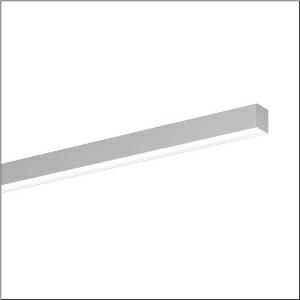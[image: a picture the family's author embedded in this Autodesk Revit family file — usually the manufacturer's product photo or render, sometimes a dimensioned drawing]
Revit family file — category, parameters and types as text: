
# Revit family: silica_21_51mx23dc4asb
name_source: partatom
category: Lighting Fixtures
units: mm (PartAtom-declared; Revit-internal decimal feet)

## family parameters
Cut with Voids When Loaded = No
Host = Face
Light Source = No
Part Type = Normal
Room Calculation Point = No
Round Connector Dimension = Use Diameter
Shared = No

## types (1)
- --- (1 x LED, 8200 lm, 58.2 W, 4000K)
    Apparent Load = 58 VA
    CIE Flux Codes = 78 96 99 100 100
    Color Rendering = 80
    Color Temperature = 4000K
    Default Elevation = 1800 mm
    Description = Silica 21, office luminaire, primary optical cover: prismatic diffuser, of PMMA, CAT 2 (L<= 3000cd/m²), light emission: direct distribution, primary light characteristic: symmetric, installation type: surface-mounted, LED, rated luminous flux: 8.200lm, luminous efficacy: 141lm/W, light colour: 840, colour temperature: 4000K, control gear: DALI 2, with terminal, 3+2-pole, max. 2.5mm², mains connection: 220..240V, AC, 50/60Hz, rated input power: 58.2W, luminaire housing, of aluminium, metallic grey (RAL 9006), length: 3.004mm, width: 53mm, height: 53mm, protection rating (complete): IP20, insulation class (complete): insulation class I (protective earthing), certification: CE, permissible operating ambient temperature: 0..+35°C, standard: EN 50419, packaging unit: 1 piece
    Height = 53 mm
    Lamp = 1 x LED
    Lamp Light Flux = 8200 lm
    Lamp Power = 58.2 W
    Lamp count = 1
    Length = 3004 mm
    Luminous efficacy = 141 lm/W
    Manufacturer = Siteco
    ModVariant = No
    Model = 51MX23DC4ASB
    Mounting Place = Ceiling
    Mounting Type = Surface mounted
    Number of Poles = 1
    OnlyDefault = Yes
    Power Factor = 1
    Product Name = Silica 21
    Product group = office luminaire | ceiling mounted
    ProductGroupID = 301
    Protection Class = Protection class I
    Protection Degree = IP 20
    RLX_Detail_Level = 1
    RLX_Emergency_Light_Flux = 0 lm
    RLX_Emergency_Type = 0
    RLX_Emergency_Type_DB = No
    RlxData = <blob elided: 21117 chars, md5=80a6b71a>
    Socket = socket
    Standby Power = 0 W
    System Light Flux = 8200 lm
    System Power = 58 W
    Type Comments = factory setting: luminous flux: 100 % | dim-lin: 254 | 323 mA
    Type Image = l_1335933.jpg
    URL = http://relux.com
    VarID = @adj_119337
    Voltage = 0 V
    Weight = 0.00 kg
    Width = 53 mm

## geometry (parser evidence)
native form markers: Blend x4, Sweep x9
no freeform markers — native parametric forms only
